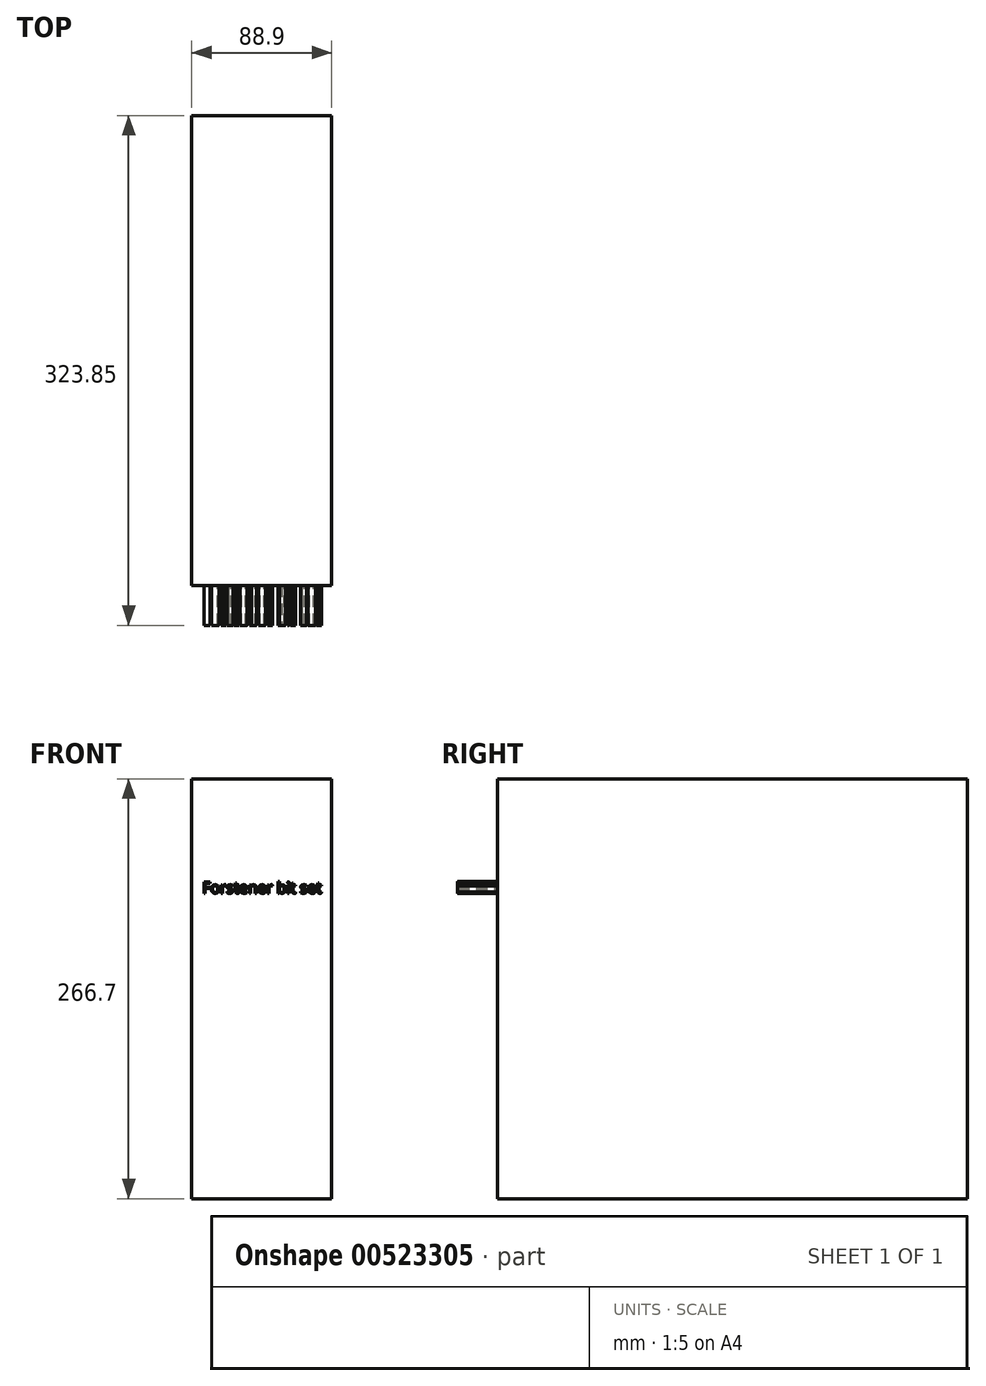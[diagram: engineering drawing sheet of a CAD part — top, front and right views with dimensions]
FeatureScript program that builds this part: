
annotation { "Feature Type Name" : "Feature", "Feature Type Description" : "" }
export const myFeature = defineFeature(function(context is Context, id is Id, definition is map)
    precondition{}
    {
        {
            var Q0;
            Q0=qCreatedBy(makeId("Front.planeOp"),FACE);
            var sketch = newSketch(context, id + "F0", { "sketchPlane" : qUnion([Q0])});
            skLineSegment(sketch, "E0.bottom", {"start": v(44.45, 133.35) * mm, "end": v(-44.45, 133.35) * mm});
            skLineSegment(sketch, "E0.top", {"start": v(44.45, -133.35) * mm, "end": v(-44.45, -133.35) * mm});
            skLineSegment(sketch, "E0.left", {"start": v(44.45, 133.35) * mm, "end": v(44.45, -133.35) * mm});
            skLineSegment(sketch, "E0.right", {"start": v(-44.45, 133.35) * mm, "end": v(-44.45, -133.35) * mm});
            skPoint(sketch, "E0.middle", {"position": v(0, 0) * mm});
            skSolve(sketch);
        }
        {
            var Q0;
            Q0=makeQuery(id+"F0.imprint","IMPRINT",FACE,{"disambiguationData":[TD([[makeQuery(id+"F0.imprint","IMPRINT",EDGE,{"derivedFrom":sQuery(id+"F0.wireOp",EDGE,"E0.bottom")}),1.0]])]});
            extrude(context, id + "F1", {"entities" : qUnion([Q0]), "depth" : 298.45 * mm, "offsetDistance" : 25.4 * mm});
        }
        {
            var Q0;
            Q0=makeQuery(id+"F1.opExtrude","CAP_FACE",FACE,{"disambiguationData":[OSD([sQuery(id+"F0.wireOp",EDGE,"E0.bottom"),sQuery(id+"F0.wireOp",EDGE,"E0.top"),sQuery(id+"F0.wireOp",EDGE,"E0.left"),sQuery(id+"F0.wireOp",EDGE,"E0.right")])],"isStart":false});
            var sketch = newSketch(context, id + "F2", { "sketchPlane" : qUnion([Q0])});
            skText(sketch, "E1", { "text": "Forstener bit set", "fontName": "OpenSans-Regular.ttf"});
            const initialGuessF2  = {"E1": [-0.03774, 0.06067, 1, 0, 0.00715]};
            skSetInitialGuess(sketch, initialGuessF2);
            skSolve(sketch);
        }
        {
            var Q0;
            Q0 = qSketchRegion(id + "F2", true);
            extrude(context, id + "F3", {"entities" : qUnion([Q0]), "operationType" : NewBodyOperationType.ADD, "depth" : 25.4 * mm, "offsetDistance" : 25.4 * mm});
        }
    });
